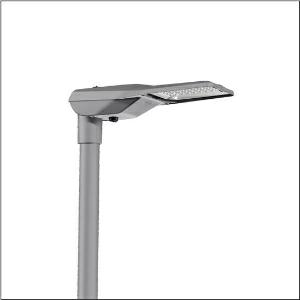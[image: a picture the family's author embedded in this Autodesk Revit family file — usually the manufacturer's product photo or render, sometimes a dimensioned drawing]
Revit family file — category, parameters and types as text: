
# Revit family: streetlight_sl_21_iq_mini___st1_0a_5xe2d41y08gb_5b29
name_source: partatom
category: Lighting Fixtures
units: mm (PartAtom-declared; Revit-internal decimal feet)

## family parameters
Cut with Voids When Loaded = No
Host = Face
Light Source = No
Part Type = Normal
Room Calculation Point = No
Round Connector Dimension = Use Diameter
Shared = No

## types (1)
- --- (1 x LED, 6190 lm, 39.8 W, 4000K)
    Apparent Load = 40 VA
    CIE Flux Codes = 37 72 97 100 100
    Color Rendering = 70
    Color Temperature = 4000K
    Default Elevation = 1800 mm
    Description = Streetlight SL 21 iQ mini, mast luminaire, primary light control with lens, of PMMA, primary optical cover: cover, of toughened safety glass, transparent, light distribution: ST1.0a, light emission: direct distribution, primary light characteristic: asymmetric, installation type: post-top, side-entry, LED, High Power LED, rated luminous flux: 6.190lm, luminous efficacy: 156lm/W, light colour: 740, colour temperature: 4000K, control: presetting dimming logarithmic, Street-Remote, Auto-Match, Temp-Guard, Lumen-Switch, Night-Set, Smart-Wire, Light-Fading, Desk-Remote (wireless, voltage-free reading and setting of iQ features in the workshop via application-optimized NFC function/RFID function), optimised constant luminous flux control (CLO 2.0), mains connection: 220..240V, AC, 50/60Hz, start of lifetime: 40W, end of service life: 41W, reduction: 18W, luminaire housing, of diecast aluminium, powder-coated, Siteco® metallic grey (DB 702S), corrosivity category C5 mid according to DIN EN ISO 12944, please order mast flange separately, inclination adjustable: 0°, 5°, 10°, 15°, sealing non-destructively replaceable, multi-level sealing system, length: 628mm, width: 235mm, height: 110mm, mast flange for spigot size: 42mm (side-entry): 5XC10008XM4, 60/48mm (side-entry/post-top): 5XC10108XM2, 76/60mm (side-entry/post-top): 5XC10108XM1, Smart Interface below and above, protection rating (complete): IP66, insulation class (complete): insulation class II (safety insulation), certification: CE, ENEC, ENEC+, VDE, impact resistance: IK09, permissible operating ambient temperature for outdoor applications: -40..+50°C, standard-compliant lighting for roads and squares, packaging unit: 1 piece

Light Distribution: ST1.0a
    Height = 110 mm
    Lamp = 1 x LED
    Lamp Light Flux = 6190 lm
    Lamp Power = 39.8 W
    Lamp count = 1
    Length = 625 mm
    Luminous efficacy = 156 lm/W
    Manufacturer = Siteco
    ModVariant = No
    Model = 5XE2D41Y08GB
    Number of Poles = 1
    OnlyDefault = Yes
    Power Factor = 1
    Product Name = Streetlight SL 21 iQ mini | ST1.0a
    Product group = mast luminaire | pylon top
    ProductGroupID = 6100
    Protection Class = Protection class II
    Protection Degree = IP 66
    RLX_Detail_Level = 1
    RLX_Emergency_Light_Flux = 0 lm
    RLX_Emergency_Type = 0
    RLX_Emergency_Type_DB = No
    RlxData = <blob elided: 92805 chars, md5=22e5f3c4>
    Socket = socket
    Standby Power = 0 W
    System Light Flux = 6190 lm
    System Power = 40 W
    Type Comments = factory setting: luminous flux: 100 % | dim-lin: 254 | 800 mA
    Type Image = l_1003514.jpg
    URL = http://relux.com
    VarID = @adj_044797
    Voltage = 0 V
    Weight = 0.00 kg
    Width = 234 mm

## geometry (parser evidence)
native form markers: Blend x4, Sweep x11
no freeform markers — native parametric forms only
